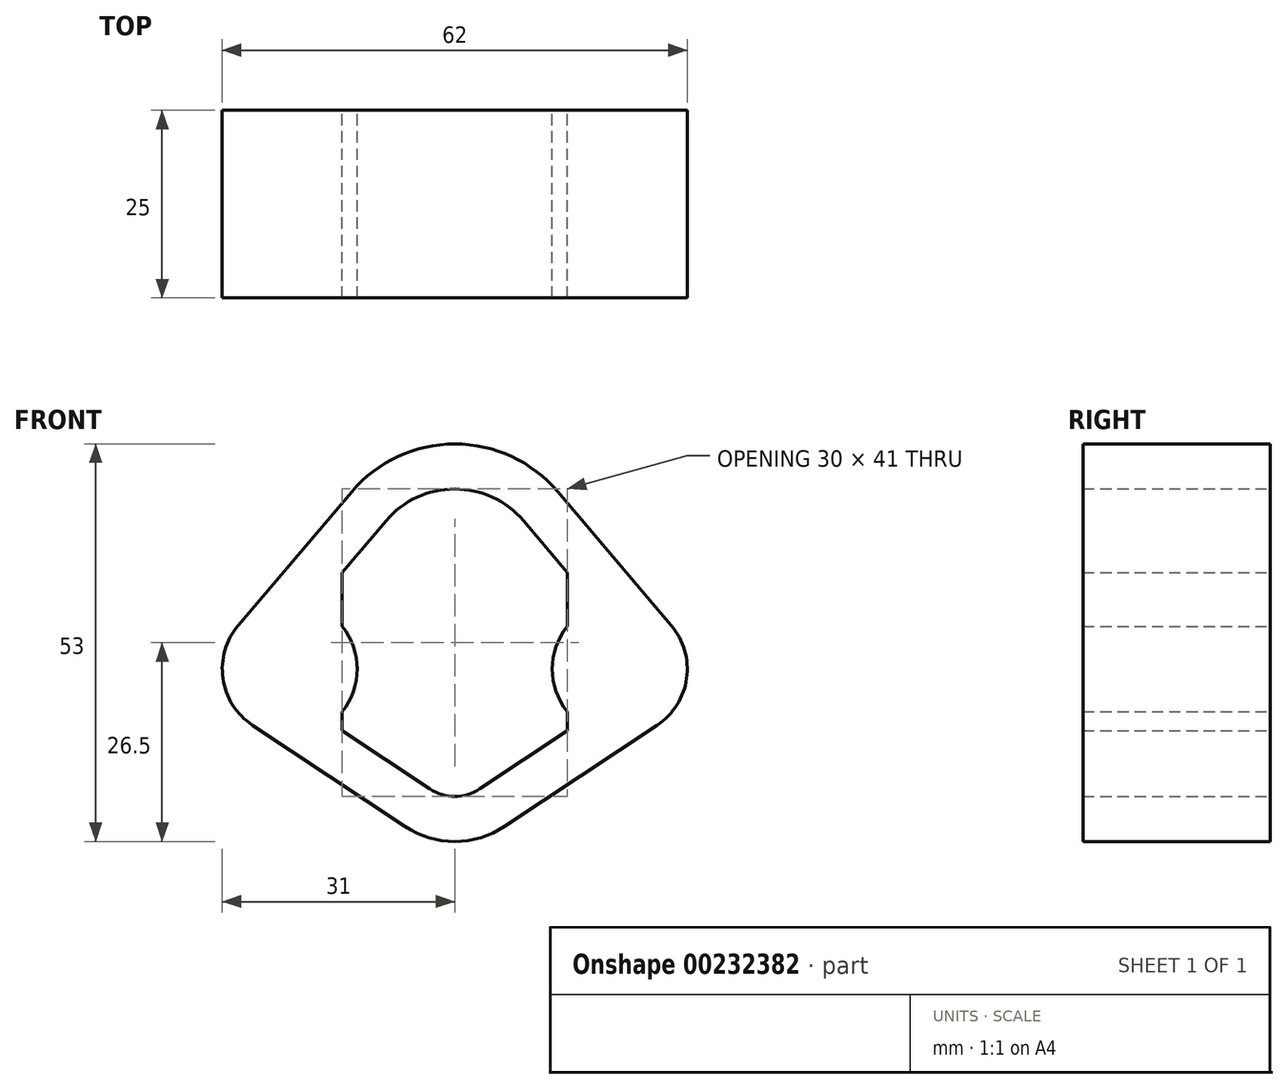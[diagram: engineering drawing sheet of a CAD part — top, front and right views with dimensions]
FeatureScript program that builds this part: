
annotation { "Feature Type Name" : "Feature", "Feature Type Description" : "" }
export const myFeature = defineFeature(function(context is Context, id is Id, definition is map)
    precondition{}
    {
        {
            var Q0;
            Q0=qCreatedBy(makeId("Front.planeOp"),FACE);
            var sketch = newSketch(context, id + "F0", { "sketchPlane" : qUnion([Q0])});
            skArc(sketch, "E0", {"start": v(15, 5.66) * mm, "mid": v(13, 0) * mm, "end": v(15, -5.66) * mm});
            skArc(sketch, "E1", {"start": v(13.72, 23.65) * mm, "mid": v(7.56, 28.34) * mm, "end": v(0, 30) * mm});
            skArc(sketch, "E2", {"start": v(6.64, -21) * mm, "mid": v(3.47, -22.49) * mm, "end": v(0, -23) * mm});
            skLineSegment(sketch, "E3", {"start": v(13.72, 23.65) * mm, "end": v(28.86, 5.83) * mm});
            skLineSegment(sketch, "E4", {"start": v(6.64, -21) * mm, "end": v(26.98, -7.5) * mm});
            skArc(sketch, "E5.0", {"start": v(9.15, 19.77) * mm, "mid": v(5.04, 22.9) * mm, "end": v(0, 24) * mm});
            skLineSegment(sketch, "E5.1", {"start": v(9.15, 19.77) * mm, "end": v(15, 12.88) * mm});
            skArc(sketch, "E6.0", {"start": v(3.32, -16) * mm, "mid": v(1.73, -16.74) * mm, "end": v(0, -17) * mm});
            skLineSegment(sketch, "E6.1", {"start": v(3.32, -16) * mm, "end": v(15, -8.25) * mm});
            skLineSegment(sketch, "E7", {"start": v(15, 12.88) * mm, "end": v(15, 5.66) * mm});
            skLineSegment(sketch, "E8.trimOffspring", {"start": v(15, -5.66) * mm, "end": v(15, -8.25) * mm});
            skArc(sketch, "E9.trimOffspring", {"start": v(26.98, -7.5) * mm, "mid": v(30.91, -1.26) * mm, "end": v(28.86, 5.83) * mm});
            skArc(sketch, "E10.MirrorCS", {"start": v(-9.15, 19.77) * mm, "mid": v(-5.04, 22.9) * mm, "end": v(0, 24) * mm});
            skArc(sketch, "E11.MirrorCS", {"start": v(-13.72, 23.65) * mm, "mid": v(-7.56, 28.34) * mm, "end": v(0, 30) * mm});
            skLineSegment(sketch, "E12.MirrorCS", {"start": v(-9.15, 19.77) * mm, "end": v(-15, 12.88) * mm});
            skLineSegment(sketch, "E13.MirrorCS", {"start": v(-13.72, 23.65) * mm, "end": v(-28.86, 5.83) * mm});
            skArc(sketch, "E14.MirrorCS", {"start": v(-26.98, -7.5) * mm, "mid": v(-30.91, -1.26) * mm, "end": v(-28.86, 5.83) * mm});
            skLineSegment(sketch, "E15.MirrorCS", {"start": v(-15, 12.88) * mm, "end": v(-15, 5.66) * mm});
            skArc(sketch, "E16.MirrorCS", {"start": v(-15, 5.66) * mm, "mid": v(-13, 0) * mm, "end": v(-15, -5.66) * mm});
            skLineSegment(sketch, "E17.MirrorCS", {"start": v(-15, -5.66) * mm, "end": v(-15, -8.25) * mm});
            skLineSegment(sketch, "E18.MirrorCS", {"start": v(-3.32, -16) * mm, "end": v(-15, -8.25) * mm});
            skArc(sketch, "E19.MirrorCS", {"start": v(-3.32, -16) * mm, "mid": v(-1.73, -16.74) * mm, "end": v(0, -17) * mm});
            skArc(sketch, "E20.MirrorCS", {"start": v(-6.64, -21) * mm, "mid": v(-3.47, -22.49) * mm, "end": v(0, -23) * mm});
            skLineSegment(sketch, "E21.MirrorCS", {"start": v(-6.64, -21) * mm, "end": v(-26.98, -7.5) * mm});
            skSolve(sketch);
        }
        {
            var Q0;
            Q0=makeQuery(id+"F0.imprint","IMPRINT",FACE,{"disambiguationData":[TD([[makeQuery(id+"F0.imprint","IMPRINT",EDGE,{"derivedFrom":sQuery(id+"F0.wireOp",EDGE,"E0")}),1.0]])]});
            extrude(context, id + "F1", {"entities" : qUnion([Q0]), "depth" : 25 * mm});
        }
    });
